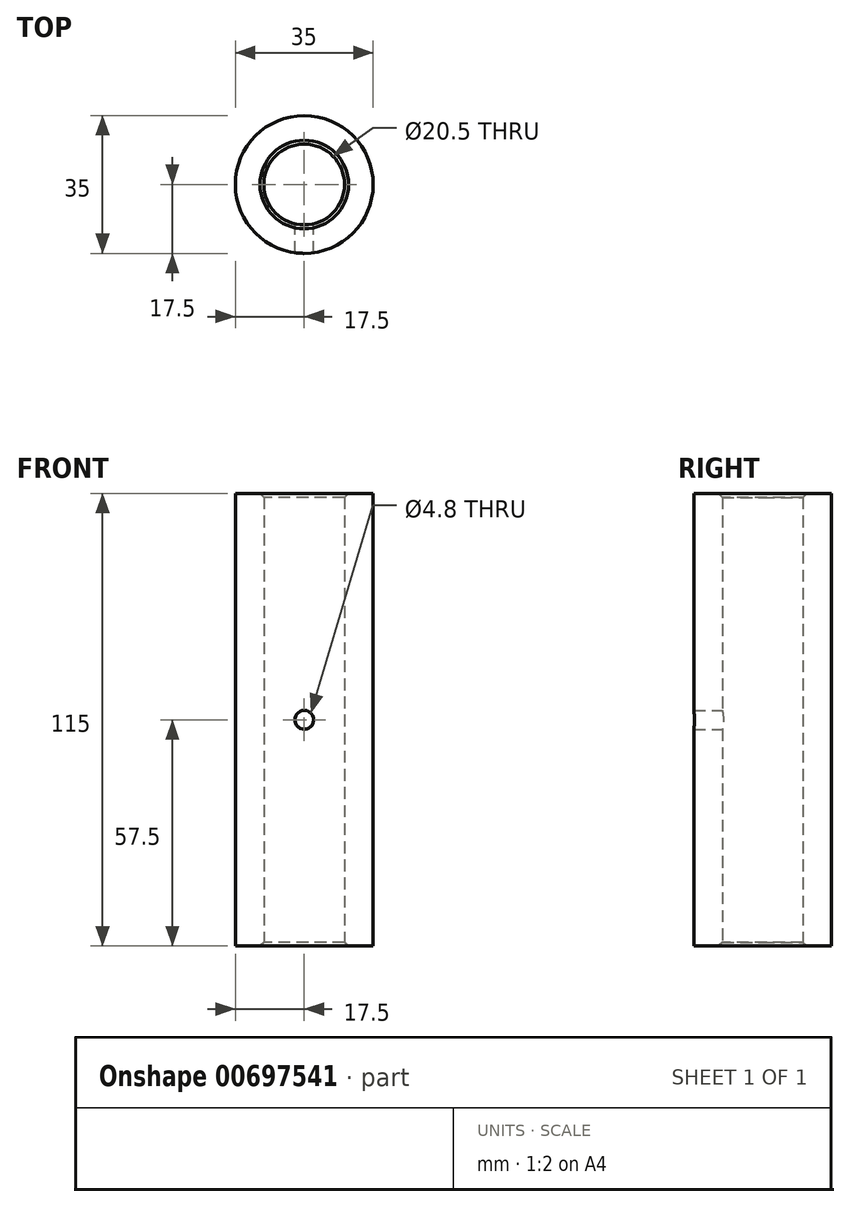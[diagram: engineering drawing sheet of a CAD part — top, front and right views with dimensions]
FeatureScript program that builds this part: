
annotation { "Feature Type Name" : "Feature", "Feature Type Description" : "" }
export const myFeature = defineFeature(function(context is Context, id is Id, definition is map)
    precondition{}
    {
        {
            var Q0;
            Q0=qCreatedBy(makeId("Top.planeOp"),FACE);
            var sketch = newSketch(context, id + "F0", { "sketchPlane" : qUnion([Q0])});
            skCircle(sketch, "E0", {"center": v(0, 0) * mm, "radius": 17.5 * mm});
            skCircle(sketch, "E1", {"center": v(0, 0) * mm, "radius": 10.25 * mm});
            skSolve(sketch);
        }
        {
            var Q0;
            Q0 = qSketchRegion(id + "F0", true);
            extrude(context, id + "F1", {"entities" : qUnion([Q0]), "endBound" : BoundingType.SYMMETRIC, "depth" : 115 * mm, "offsetDistance" : 25 * mm});
        }
        {
            var Q0;
            Q0=qCreatedBy(makeId("Front.planeOp"),FACE);
            var sketch = newSketch(context, id + "F2", { "sketchPlane" : qUnion([Q0])});
            skCircle(sketch, "E2", {"center": v(0, 0) * mm, "radius": 2.4 * mm});
            skSolve(sketch);
        }
        {
            var Q0;
            Q0 = qSketchRegion(id + "F2", true);
            extrude(context, id + "F3", {"entities" : qUnion([Q0]), "operationType" : NewBodyOperationType.REMOVE, "depth" : 25 * mm, "offsetDistance" : 25 * mm});
        }
        {
            var Q0;
            Q0=makeQuery(id+"F1.opExtrude","CAP_EDGE",EDGE,{"disambiguationData":[OSD([sQuery(id+"F0.wireOp",EDGE,"E1")])],"isStart":false});
            chamfer(context, id + "F4", {"entities" : qUnion([Q0]), "width" : 1 * mm, "tangentPropagation" : true});
        }
        {
            var Q0;
            Q0=makeQuery(id+"F1.opExtrude","CAP_EDGE",EDGE,{"disambiguationData":[OSD([sQuery(id+"F0.wireOp",EDGE,"E1")])],"isStart":true});
            chamfer(context, id + "F5", {"entities" : qUnion([Q0]), "width" : 1 * mm, "tangentPropagation" : true});
        }
    });
